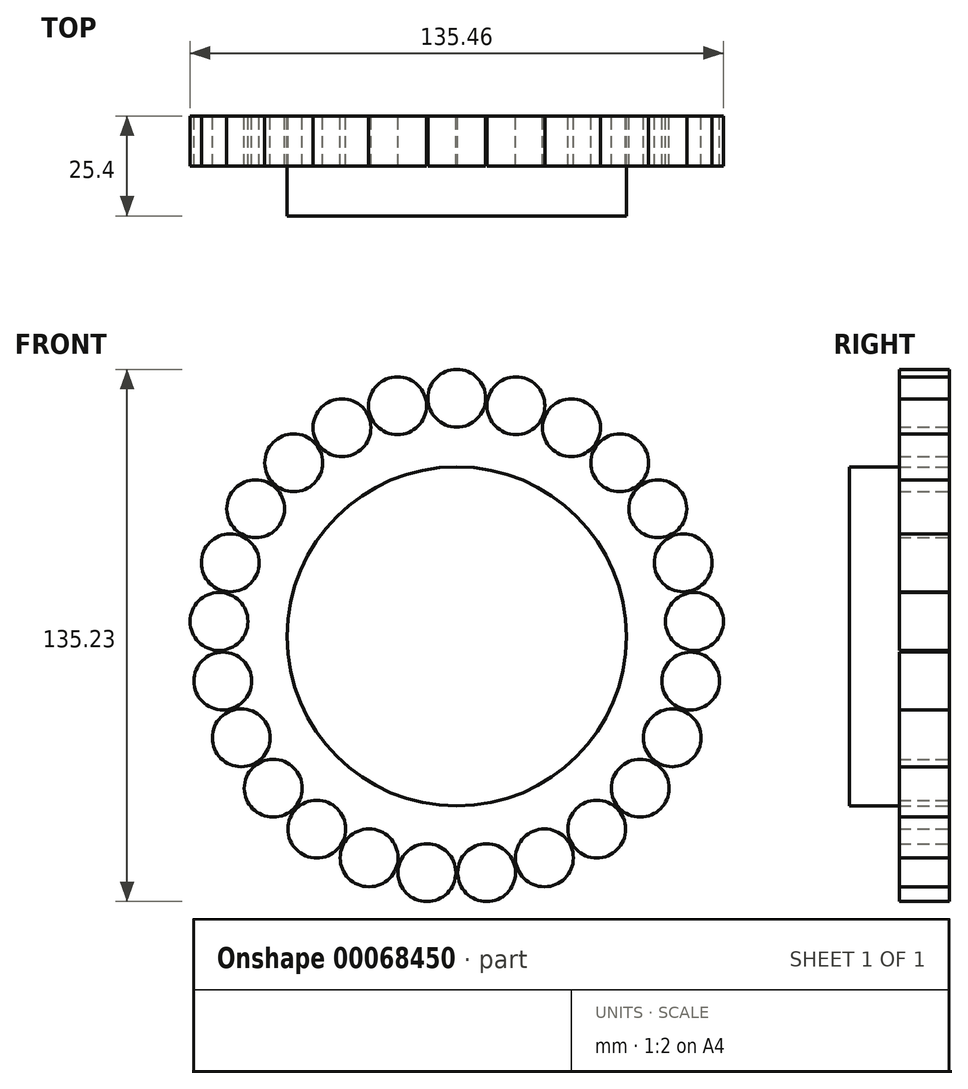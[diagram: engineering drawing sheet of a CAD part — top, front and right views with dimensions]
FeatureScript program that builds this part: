
annotation { "Feature Type Name" : "Feature", "Feature Type Description" : "" }
export const myFeature = defineFeature(function(context is Context, id is Id, definition is map)
    precondition{}
    {
        {
            var Q0;
            Q0=qCreatedBy(makeId("Front.planeOp"),FACE);
            var sketch = newSketch(context, id + "F0", { "sketchPlane" : qUnion([Q0])});
            skCircle(sketch, "E0", {"center": v(0, 0) * mm, "radius": 43.1 * mm});
            skCircle(sketch, "E1", {"center": v(-63.72, 58.77) * mm, "radius": 26.33 * mm});
            skSolve(sketch);
        }
        {
            var Q0;
            Q0=makeQuery(id+"F0.imprint","IMPRINT",FACE,{"disambiguationData":[TD([[makeQuery(id+"F0.imprint","IMPRINT",EDGE,{"derivedFrom":sQuery(id+"F0.wireOp",EDGE,"E0")}),1.0]])]});
            extrude(context, id + "F1", {"entities" : qUnion([Q0]), "depth" : 25.4 * mm});
        }
        {
            var Q0;
            Q0=qCreatedBy(makeId("Front.planeOp"),FACE);
            var sketch = newSketch(context, id + "F2", { "sketchPlane" : qUnion([Q0])});
            skCircle(sketch, "E2", {"center": v(0, 60.5) * mm, "radius": 7.35 * mm});
            skSolve(sketch);
        }
        {
            var Q0;
            Q0=makeQuery(id+"F2.imprint","IMPRINT",FACE,{"disambiguationData":[TD([[makeQuery(id+"F2.imprint","IMPRINT",EDGE,{"derivedFrom":sQuery(id+"F2.wireOp",EDGE,"E2")}),1.0]])]});
            extrude(context, id + "F3", {"entities" : qUnion([Q0]), "depth" : 12.7 * mm});
        }
        {
            var Q0;
            Q0=makeQuery(id+"F3.opExtrude","SWEPT_BODY",BODY,{"disambiguationData":[OSD([sQuery(id+"F2.wireOp",EDGE,"E2")])]});
            var Q1;
            Q1=makeQuery(id+"F1.opExtrude","CAP_EDGE",EDGE,{"disambiguationData":[OSD([sQuery(id+"F0.wireOp",EDGE,"E0")])],"isStart":false});
            circularPattern(context, id + "F4", {"entities" : qUnion([Q0]), "axis" : qUnion([Q1]), "angle" : 360 * degree, "instanceCount" : 25, "oppositeDirection" : true, "equalSpace" : true});
        }
    });
